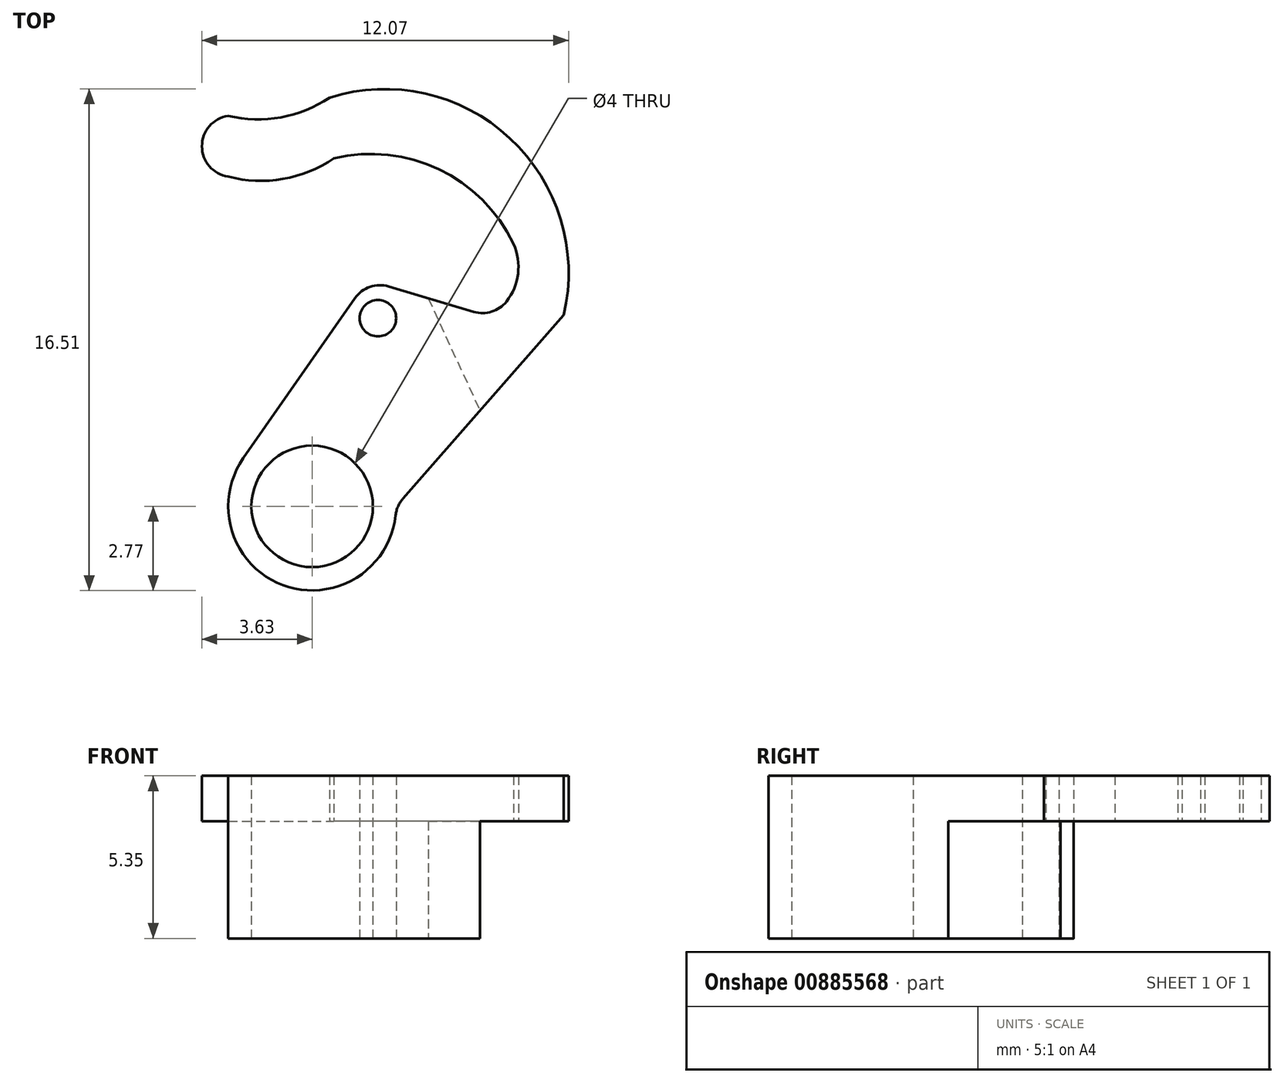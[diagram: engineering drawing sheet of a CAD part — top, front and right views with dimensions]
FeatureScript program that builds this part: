
annotation { "Feature Type Name" : "Feature", "Feature Type Description" : "" }
export const myFeature = defineFeature(function(context is Context, id is Id, definition is map)
    precondition{}
    {
        {
            var Q0;
            Q0=qCreatedBy(makeId("Top.planeOp"),FACE);
            var sketch = newSketch(context, id + "F0", { "sketchPlane" : qUnion([Q0])});
            skCircle(sketch, "E0", {"center": v(0, 0) * mm, "radius": 2 * mm});
            skCircle(sketch, "E1", {"center": v(0, 0) * mm, "radius": 2.77 * mm, "construction": true});
            skCircle(sketch, "E2", {"center": v(2.17, 6.2) * mm, "radius": 0.6 * mm});
            skLineSegment(sketch, "E3", {"start": v(-2.77, 6.8) * mm, "end": v(2.76, 6.8) * mm, "construction": true});
            skLineSegment(sketch, "E4", {"start": v(2.77, 0) * mm, "end": v(2.77, 6.8) * mm});
            skArc(sketch, "E5", {"start": v(-2.77, 0) * mm, "mid": v(0, -2.76) * mm, "end": v(2.77, 0) * mm, "construction": true});
            skLineSegment(sketch, "E6", {"start": v(0.82, 4.3) * mm, "end": v(3.51, 4.3) * mm, "construction": true});
            skLineSegment(sketch, "E7", {"start": v(2.17, 6.2) * mm, "end": v(2.17, 4.3) * mm, "construction": true});
            skLineSegment(sketch, "E8", {"start": v(-1.45, 2.35) * mm, "end": v(5.82, 6.26) * mm, "construction": true});
            skArc(sketch, "E9", {"start": v(5.82, 6.26) * mm, "mid": v(6.7, 7.28) * mm, "end": v(6.63, 8.63) * mm});
            skArc(sketch, "E10", {"start": v(6.63, 8.63) * mm, "mid": v(4.17, 11.1) * mm, "end": v(0.7, 11.45) * mm});
            skArc(sketch, "E11", {"start": v(-2.76, 10.85) * mm, "mid": v(-0.96, 10.78) * mm, "end": v(0.7, 11.45) * mm});
            skLineSegment(sketch, "E12", {"start": v(-2.77, 0) * mm, "end": v(-2.77, 10.85) * mm, "construction": true});
            skArc(sketch, "E13", {"start": v(-2.77, 12.85) * mm, "mid": v(-3.63, 11.85) * mm, "end": v(-2.76, 10.85) * mm});
            skArc(sketch, "E14", {"start": v(-2.76, 12.85) * mm, "mid": v(-1.03, 12.8) * mm, "end": v(0.57, 13.45) * mm});
            skLineSegment(sketch, "E15", {"start": v(8.28, 6.3) * mm, "end": v(2.76, 0) * mm});
            skArc(sketch, "E16", {"start": v(8.28, 6.3) * mm, "mid": v(6.5, 12.12) * mm, "end": v(0.57, 13.45) * mm});
            skLineSegment(sketch, "E17", {"start": v(5.82, 6.26) * mm, "end": v(1.83, 7.45) * mm});
            skLineSegment(sketch, "E18", {"start": v(1.83, 7.45) * mm, "end": v(-2.27, 1.58) * mm});
            skArc(sketch, "E19", {"start": v(-2.27, 1.58) * mm, "mid": v(-0.83, -2.64) * mm, "end": v(2.77, 0) * mm});
            skLineSegment(sketch, "E20", {"start": v(3.82, 6.85) * mm, "end": v(5.52, 3.15) * mm});
            skSolve(sketch);
        }
        {
            var Q0;
            Q0=makeQuery(id+"F0.imprint","IMPRINT",FACE,{"disambiguationData":[TD([[makeQuery(id+"F0.imprint","IMPRINT",EDGE,{"derivedFrom":sQuery(id+"F0.wireOp",EDGE,"E0")}),-1.0]])]});
            var Q1;
            {var subQ1=sQuery(id+"F0.wireOp",EDGE,"E9");Q1=makeQuery(id+"F0.imprint","IMPRINT",FACE,{"disambiguationData":[TD([[makeQuery(id+"F0.imprint","IMPRINT",EDGE,{"derivedFrom":subQ1}),-1.0]])]});}
            extrude(context, id + "F1", {"entities" : qUnion([Q0, Q1]), "depth" : 5.35 * mm, "offsetDistance" : 25 * mm});
        }
        {
            var Q0;
            {var subQ1=sQuery(id+"F0.wireOp",EDGE,"E9");Q0=makeQuery(id+"F0.imprint","IMPRINT",FACE,{"disambiguationData":[TD([[makeQuery(id+"F0.imprint","IMPRINT",EDGE,{"derivedFrom":subQ1}),-1.0]])]});}
            extrude(context, id + "F2", {"entities" : qUnion([Q0]), "operationType" : NewBodyOperationType.REMOVE, "depth" : 3.85 * mm, "offsetDistance" : 25 * mm});
        }
        {
            var Q0;
            Q0=makeQuery(id+"F1.opExtrude","SWEPT_EDGE",EDGE,{"disambiguationData":[OSD([sQuery(id+"F0.wireOp",EDGE,"E17"),sQuery(id+"F0.wireOp",EDGE,"E18")])]});
            var Q1;
            Q1=makeQuery(id+"F2.boolean.opBoolean","COPY",EDGE,{"derivedFrom":makeQuery(id+"F2.opExtrude","SWEPT_EDGE",EDGE,{"disambiguationData":[OSD([sQuery(id+"F0.wireOp",EDGE,"E17"),sQuery(id+"F0.wireOp",EDGE,"E20")])]})});
            var Q2;
            Q2=makeQuery(id+"F1.opExtrude","SWEPT_EDGE",EDGE,{"disambiguationData":[OSD([sQuery(id+"F0.wireOp",EDGE,"E9"),sQuery(id+"F0.wireOp",EDGE,"E17")])]});
            var Q3;
            Q3=makeQuery(id+"F2.boolean.opBoolean","COPY",EDGE,{"derivedFrom":makeQuery(id+"F2.opExtrude","SWEPT_EDGE",EDGE,{"disambiguationData":[OSD([sQuery(id+"F0.wireOp",EDGE,"E15"),sQuery(id+"F0.wireOp",EDGE,"E20")])]})});
            var Q4;
            Q4=makeQuery(id+"F1.opExtrude","SWEPT_EDGE",EDGE,{"disambiguationData":[OSD([sQuery(id+"F0.wireOp",EDGE,"E15"),sQuery(id+"F0.wireOp",EDGE,"E19")])]});
            fillet(context, id + "F3", {"entities" : qUnion([Q0, Q1, Q2, Q3, Q4]), "radius" : 1 * mm, "tangentPropagation" : true, "allowEdgeOverflow" : false});
        }
    });
